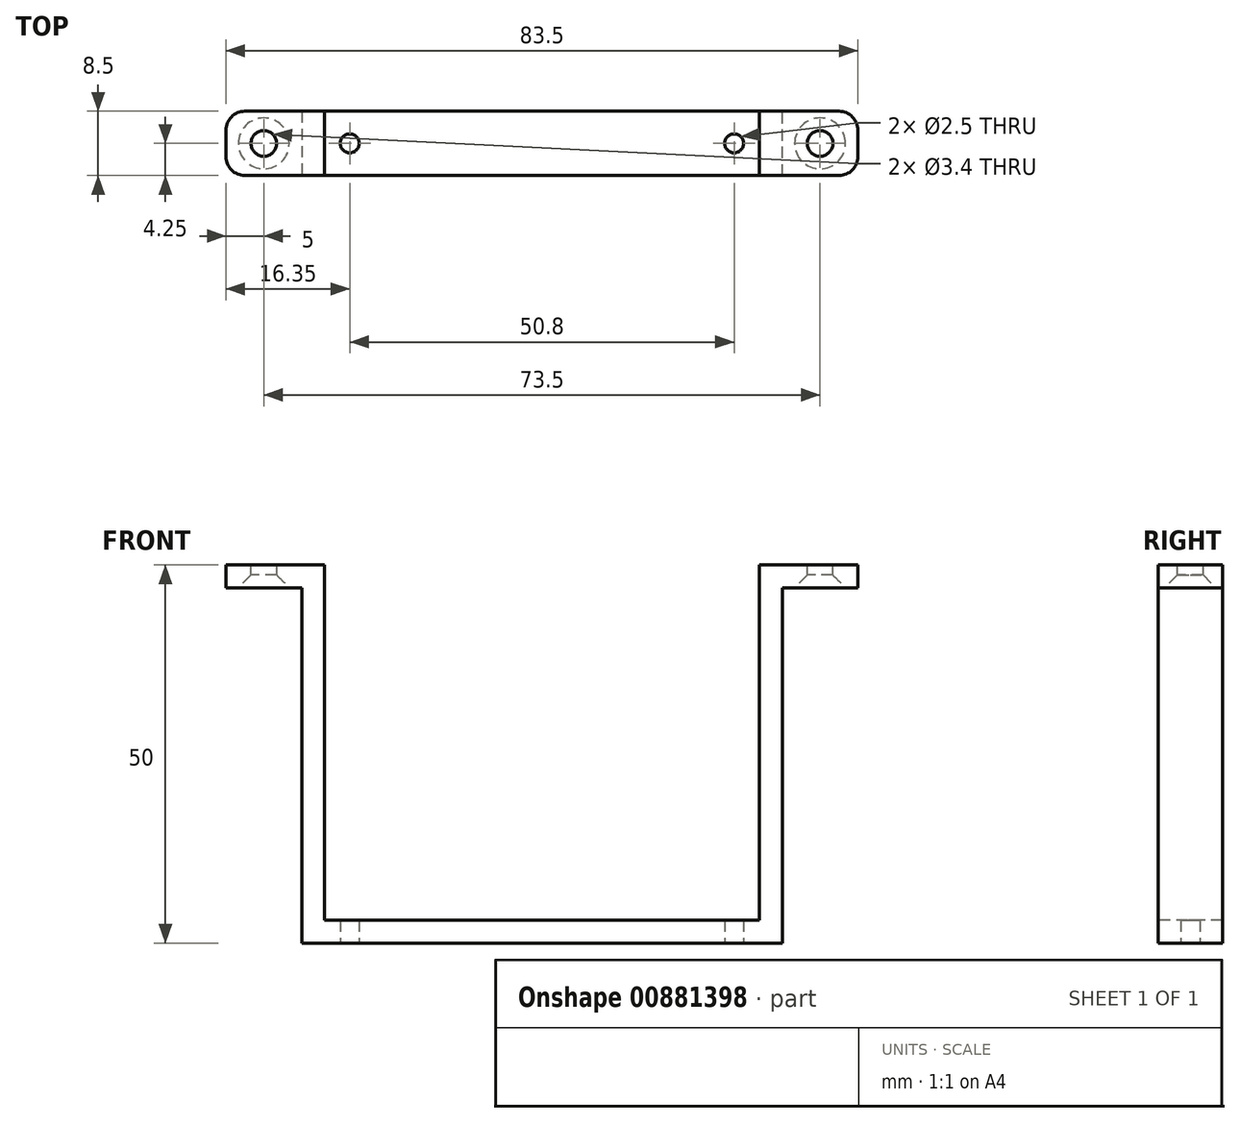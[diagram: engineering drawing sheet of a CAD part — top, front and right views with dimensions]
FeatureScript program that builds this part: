
annotation { "Feature Type Name" : "Feature", "Feature Type Description" : "" }
export const myFeature = defineFeature(function(context is Context, id is Id, definition is map)
    precondition{}
    {
        {
            var Q0;
            Q0=qCreatedBy(makeId("Top.planeOp"),FACE);
            var sketch = newSketch(context, id + "F0", { "sketchPlane" : qUnion([Q0])});
            skLineSegment(sketch, "E0.bottom", {"start": v(31.75, -4.25) * mm, "end": v(-31.75, -4.25) * mm});
            skLineSegment(sketch, "E0.top", {"start": v(31.75, 4.25) * mm, "end": v(-31.75, 4.25) * mm});
            skLineSegment(sketch, "E0.left", {"start": v(31.75, -4.25) * mm, "end": v(31.75, 4.25) * mm});
            skLineSegment(sketch, "E0.right", {"start": v(-31.75, -4.25) * mm, "end": v(-31.75, 4.25) * mm});
            skPoint(sketch, "E0.middle", {"position": v(0, 0) * mm});
            skPoint(sketch, "E1", {"position": v(25.4, 0) * mm});
            skPoint(sketch, "E2", {"position": v(-25.4, 0) * mm});
            skCircle(sketch, "E3", {"center": v(-25.4, 0) * mm, "radius": 1.25 * mm});
            skCircle(sketch, "E4", {"center": v(25.4, 0) * mm, "radius": 1.25 * mm});
            skSolve(sketch);
        }
        {
            var Q0;
            Q0=makeQuery(id+"F0.imprint","IMPRINT",FACE,{"disambiguationData":[TD([[makeQuery(id+"F0.imprint","IMPRINT",EDGE,{"derivedFrom":sQuery(id+"F0.wireOp",EDGE,"E0.bottom")}),-1.0]])]});
            extrude(context, id + "F1", {"entities" : qUnion([Q0]), "depth" : 3 * mm, "offsetDistance" : 25 * mm});
        }
        {
            var Q0;
            Q0=makeQuery(id+"F1.opExtrude","CAP_FACE",FACE,{"disambiguationData":[OSD([sQuery(id+"F0.wireOp",EDGE,"E0.bottom"),sQuery(id+"F0.wireOp",EDGE,"E0.top"),sQuery(id+"F0.wireOp",EDGE,"E0.left"),sQuery(id+"F0.wireOp",EDGE,"E0.right"),sQuery(id+"F0.wireOp",EDGE,"E3"),sQuery(id+"F0.wireOp",EDGE,"E4")])],"isStart":false});
            var sketch = newSketch(context, id + "F2", { "sketchPlane" : qUnion([Q0])});
            skPoint(sketch, "E5", {"position": v(28.75, 4.25) * mm});
            skPoint(sketch, "E6", {"position": v(28.75, -4.25) * mm});
            skPoint(sketch, "E7", {"position": v(-28.75, 4.25) * mm});
            skPoint(sketch, "E8", {"position": v(-28.75, -4.25) * mm});
            skLineSegment(sketch, "E9", {"start": v(-28.75, 4.25) * mm, "end": v(-28.75, -4.25) * mm});
            skLineSegment(sketch, "E10", {"start": v(28.75, 4.25) * mm, "end": v(28.75, -4.25) * mm});
            skSolve(sketch);
        }
        {
            var Q0;
            {var subQ0=sQuery(id+"F2.wireOp",EDGE,"E9");Q0=makeQuery(id+"F2.imprint","IMPRINT",FACE,{"disambiguationData":[TD([[makeQuery(id+"F2.imprint","IMPRINT",EDGE,{"derivedFrom":subQ0}),-1.0]])]});}
            var Q1;
            {var subQ0=sQuery(id+"F2.wireOp",EDGE,"E10");Q1=makeQuery(id+"F2.imprint","IMPRINT",FACE,{"disambiguationData":[TD([[makeQuery(id+"F2.imprint","IMPRINT",EDGE,{"derivedFrom":subQ0}),1.0]])]});}
            extrude(context, id + "F3", {"entities" : qUnion([Q0, Q1]), "operationType" : NewBodyOperationType.ADD, "depth" : 47 * mm, "offsetDistance" : 25 * mm});
        }
        {
            var Q0;
            {var subQ0=sQuery(id+"F0.wireOp",EDGE,"E0.right");Q0=makeQuery(id+"F3.boolean.opBoolean","MERGE",FACE,{"derivedFrom":[makeQuery(id+"F1.opExtrude","SWEPT_FACE",FACE,{"disambiguationData":[OSD([subQ0])]}),makeQuery(id+"F3.opExtrude","SWEPT_FACE",FACE,{"disambiguationData":[OSD([subQ0])]})]});}
            var sketch = newSketch(context, id + "F4", { "sketchPlane" : qUnion([Q0])});
            skPoint(sketch, "E11", {"position": v(-4.25, 47) * mm});
            skPoint(sketch, "E12", {"position": v(4.25, 47) * mm});
            skLineSegment(sketch, "E13", {"start": v(-4.25, 47) * mm, "end": v(4.25, 47) * mm});
            skSolve(sketch);
        }
        {
            var Q0;
            {var subQ0=sQuery(id+"F4.wireOp",EDGE,"E13");Q0=makeQuery(id+"F4.imprint","IMPRINT",FACE,{"disambiguationData":[TD([[makeQuery(id+"F4.imprint","IMPRINT",EDGE,{"derivedFrom":subQ0}),1.0]])]});}
            extrude(context, id + "F5", {"entities" : qUnion([Q0]), "operationType" : NewBodyOperationType.ADD, "depth" : 10 * mm, "offsetDistance" : 25 * mm});
        }
        {
            var Q0;
            {var subQ0=sQuery(id+"F0.wireOp",EDGE,"E0.left");Q0=makeQuery(id+"F3.boolean.opBoolean","MERGE",FACE,{"derivedFrom":[makeQuery(id+"F1.opExtrude","SWEPT_FACE",FACE,{"disambiguationData":[OSD([subQ0])]}),makeQuery(id+"F3.opExtrude","SWEPT_FACE",FACE,{"disambiguationData":[OSD([subQ0])]})]});}
            var sketch = newSketch(context, id + "F6", { "sketchPlane" : qUnion([Q0])});
            skPoint(sketch, "E14", {"position": v(-4.25, 47) * mm});
            skPoint(sketch, "E15", {"position": v(4.25, 47) * mm});
            skLineSegment(sketch, "E16", {"start": v(-4.25, 47) * mm, "end": v(4.25, 47) * mm});
            skSolve(sketch);
        }
        {
            var Q0;
            {var subQ0=sQuery(id+"F6.wireOp",EDGE,"E16");Q0=makeQuery(id+"F6.imprint","IMPRINT",FACE,{"disambiguationData":[TD([[makeQuery(id+"F6.imprint","IMPRINT",EDGE,{"derivedFrom":subQ0}),1.0]])]});}
            extrude(context, id + "F7", {"entities" : qUnion([Q0]), "operationType" : NewBodyOperationType.ADD, "depth" : 10 * mm, "offsetDistance" : 25 * mm});
        }
        {
            var Q0;
            Q0=makeQuery(id+"F5.opExtrude","SWEPT_FACE",FACE,{"disambiguationData":[OSD([sQuery(id+"F4.wireOp",EDGE,"E13")])]});
            var sketch = newSketch(context, id + "F8", { "sketchPlane" : qUnion([Q0])});
            skPoint(sketch, "E17", {"position": v(-36.75, 0) * mm});
            skPoint(sketch, "E17.positionSnap0", {"position": v(-36.75, 4.25) * mm});
            skSolve(sketch);
        }
        {
            var Q0;
            Q0=sQuery(id+"F8.wireOp",VERTEX,"E17");
            var Q1;
            Q1=makeQuery(id+"F1.opExtrude","SWEPT_BODY",BODY,{"disambiguationData":[OSD([sQuery(id+"F0.wireOp",EDGE,"E0.bottom"),sQuery(id+"F0.wireOp",EDGE,"E0.top"),sQuery(id+"F0.wireOp",EDGE,"E0.left"),sQuery(id+"F0.wireOp",EDGE,"E0.right"),sQuery(id+"F0.wireOp",EDGE,"E3"),sQuery(id+"F0.wireOp",EDGE,"E4")])]});
            hole(context, id + "F9", {"style" : HoleStyle.C_SINK, "endStyle" : HoleEndStyle.BLIND, "standardTappedOrClearance" : lookupTablePath({ "fit" : "Normal", "standard" : "ISO", "size" : "M3", "type" : "Clearance" }), "standardBlindInLast" : lookupTablePath({ "fit" : "Normal", "standard" : "ISO", "size" : "M3", "type" : "Clearance" }), "holeDiameter" : 3.4 * mm, "cSinkDiameter" : 6.72 * mm, "cSinkAngle" : 90 * degree, "majorDiameter" : 5 * mm, "holeDepth" : 5 * mm, "isTappedThrough" : true, "tappedDepth" : 12 * mm, "tapClearance" : 3, "locations" : qUnion([Q0]), "scope" : qUnion([Q1]), "startStyle" : HoleStartStyle.SKETCH});
        }
        {
            var Q0;
            Q0=makeQuery(id+"F7.opExtrude","SWEPT_FACE",FACE,{"disambiguationData":[OSD([sQuery(id+"F6.wireOp",EDGE,"E16")])]});
            var sketch = newSketch(context, id + "F10", { "sketchPlane" : qUnion([Q0])});
            skPoint(sketch, "E18", {"position": v(36.75, 0) * mm});
            skPoint(sketch, "E18.positionSnap0", {"position": v(36.75, 4.25) * mm});
            skPoint(sketch, "E18.positionSnap1", {"position": v(41.75, 0) * mm});
            skSolve(sketch);
        }
        {
            var Q0;
            Q0=sQuery(id+"F10.wireOp",VERTEX,"E18");
            var Q1;
            Q1=makeQuery(id+"F1.opExtrude","SWEPT_BODY",BODY,{"disambiguationData":[OSD([sQuery(id+"F0.wireOp",EDGE,"E0.bottom"),sQuery(id+"F0.wireOp",EDGE,"E0.top"),sQuery(id+"F0.wireOp",EDGE,"E0.left"),sQuery(id+"F0.wireOp",EDGE,"E0.right"),sQuery(id+"F0.wireOp",EDGE,"E3"),sQuery(id+"F0.wireOp",EDGE,"E4")])]});
            hole(context, id + "F11", {"style" : HoleStyle.C_SINK, "endStyle" : HoleEndStyle.BLIND, "standardTappedOrClearance" : lookupTablePath({ "fit" : "Normal", "standard" : "ISO", "size" : "M3", "type" : "Clearance" }), "standardBlindInLast" : lookupTablePath({ "fit" : "Normal", "standard" : "ISO", "size" : "M3", "type" : "Clearance" }), "holeDiameter" : 3.4 * mm, "cSinkDiameter" : 6.72 * mm, "cSinkAngle" : 90 * degree, "majorDiameter" : 5 * mm, "holeDepth" : 5 * mm, "isTappedThrough" : true, "tappedDepth" : 12 * mm, "tapClearance" : 3, "locations" : qUnion([Q0]), "scope" : qUnion([Q1]), "startStyle" : HoleStartStyle.SKETCH});
        }
        {
            var Q0;
            Q0=makeQuery(id+"F7.opExtrude","CAP_EDGE",EDGE,{"disambiguationData":[OSD([sQuery(id+"F0.wireOp",EDGE,"E0.top"),sQuery(id+"F0.wireOp",EDGE,"E0.left")])],"isStart":false});
            var Q1;
            Q1=makeQuery(id+"F7.opExtrude","CAP_EDGE",EDGE,{"disambiguationData":[OSD([sQuery(id+"F0.wireOp",EDGE,"E0.bottom"),sQuery(id+"F0.wireOp",EDGE,"E0.left")])],"isStart":false});
            var Q2;
            Q2=makeQuery(id+"F5.opExtrude","CAP_EDGE",EDGE,{"disambiguationData":[OSD([sQuery(id+"F0.wireOp",EDGE,"E0.top"),sQuery(id+"F0.wireOp",EDGE,"E0.right")])],"isStart":false});
            var Q3;
            Q3=makeQuery(id+"F5.opExtrude","CAP_EDGE",EDGE,{"disambiguationData":[OSD([sQuery(id+"F0.wireOp",EDGE,"E0.bottom"),sQuery(id+"F0.wireOp",EDGE,"E0.right")])],"isStart":false});
            fillet(context, id + "F12", {"entities" : qUnion([Q0, Q1, Q2, Q3]), "radius" : 2.5 * mm, "tangentPropagation" : true, "allowEdgeOverflow" : false});
        }
    });
